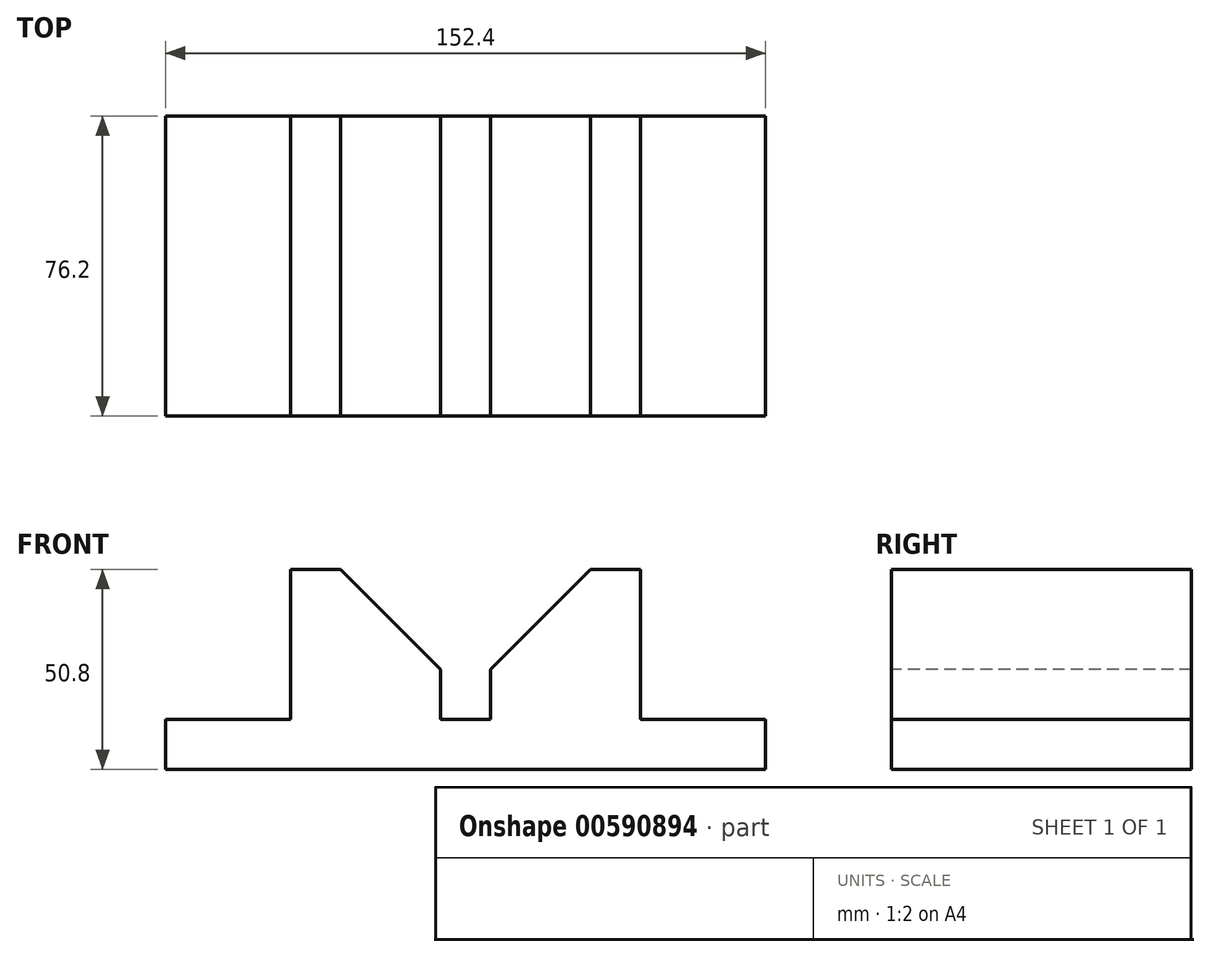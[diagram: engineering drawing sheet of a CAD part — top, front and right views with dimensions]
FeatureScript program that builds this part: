
annotation { "Feature Type Name" : "Feature", "Feature Type Description" : "" }
export const myFeature = defineFeature(function(context is Context, id is Id, definition is map)
    precondition{}
    {
        {
            var Q0;
            Q0=qCreatedBy(makeId("Front.planeOp"),FACE);
            var sketch = newSketch(context, id + "F0", { "sketchPlane" : qUnion([Q0])});
            skLineSegment(sketch, "E0", {"start": v(0, 0) * mm, "end": v(0, 12.7) * mm});
            skLineSegment(sketch, "E1", {"start": v(0, 12.7) * mm, "end": v(31.75, 12.7) * mm});
            skLineSegment(sketch, "E2", {"start": v(31.75, 12.7) * mm, "end": v(31.75, 50.8) * mm});
            skLineSegment(sketch, "E3", {"start": v(31.75, 50.8) * mm, "end": v(44.45, 50.8) * mm});
            skLineSegment(sketch, "E4", {"start": v(44.45, 50.8) * mm, "end": v(69.85, 25.4) * mm});
            skLineSegment(sketch, "E5", {"start": v(69.85, 25.4) * mm, "end": v(69.85, 12.7) * mm});
            skLineSegment(sketch, "E6", {"start": v(69.85, 12.7) * mm, "end": v(82.55, 12.7) * mm});
            skLineSegment(sketch, "E7", {"start": v(82.55, 12.7) * mm, "end": v(82.55, 25.4) * mm});
            skLineSegment(sketch, "E8", {"start": v(82.55, 25.4) * mm, "end": v(107.95, 50.8) * mm});
            skLineSegment(sketch, "E9", {"start": v(107.95, 50.8) * mm, "end": v(120.65, 50.8) * mm});
            skLineSegment(sketch, "E10", {"start": v(120.65, 50.8) * mm, "end": v(120.65, 12.7) * mm});
            skLineSegment(sketch, "E11", {"start": v(120.65, 12.7) * mm, "end": v(152.4, 12.7) * mm});
            skLineSegment(sketch, "E12", {"start": v(152.4, 12.7) * mm, "end": v(152.4, 0) * mm});
            skLineSegment(sketch, "E13", {"start": v(152.4, 0) * mm, "end": v(0, 0) * mm});
            skSolve(sketch);
        }
        {
            var Q0;
            Q0 = qSketchRegion(id + "F0", true);
            extrude(context, id + "F1", {"entities" : qUnion([Q0]), "oppositeDirection" : true, "depth" : 76.2 * mm, "offsetDistance" : 25.4 * mm});
        }
    });
